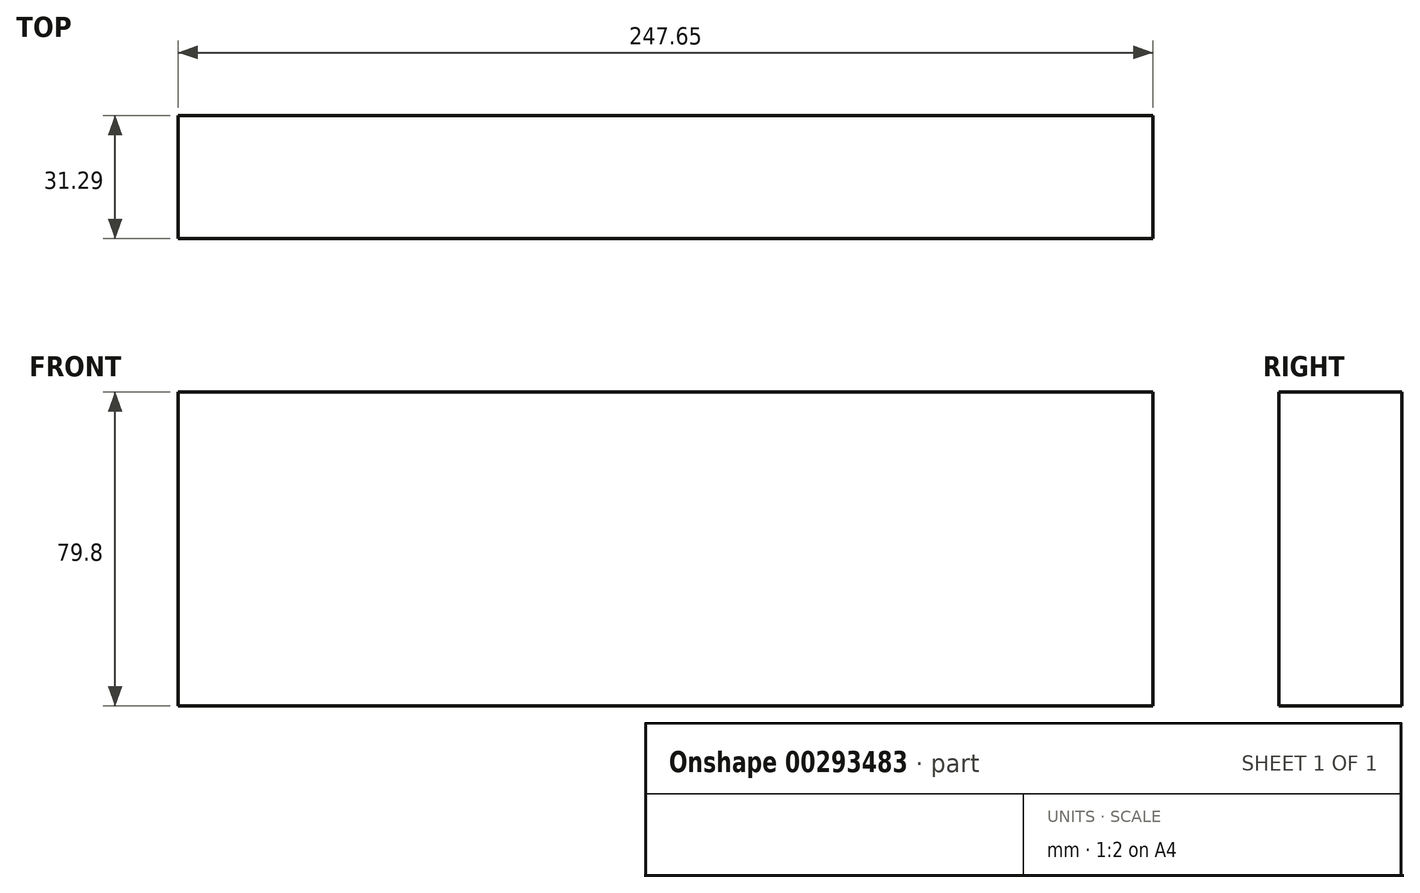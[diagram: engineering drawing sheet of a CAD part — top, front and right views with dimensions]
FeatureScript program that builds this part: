
annotation { "Feature Type Name" : "Feature", "Feature Type Description" : "" }
export const myFeature = defineFeature(function(context is Context, id is Id, definition is map)
    precondition{}
    {
        {
            var Q0;
            Q0=qCreatedBy(makeId("Front.planeOp"),FACE);
            var sketch = newSketch(context, id + "F0", { "sketchPlane" : qUnion([Q0])});
            skLineSegment(sketch, "E0.bottom", {"start": v(-81.04, 33.4) * mm, "end": v(166.6, 33.4) * mm});
            skLineSegment(sketch, "E0.top", {"start": v(-81.04, -46.41) * mm, "end": v(166.6, -46.41) * mm});
            skLineSegment(sketch, "E0.left", {"start": v(-81.04, 33.4) * mm, "end": v(-81.04, -46.41) * mm});
            skLineSegment(sketch, "E0.right", {"start": v(166.6, 33.4) * mm, "end": v(166.6, -46.41) * mm});
            skSolve(sketch);
        }
        {
            var Q0;
            Q0 = qSketchRegion(id + "F0", true);
            extrude(context, id + "F1", {"entities" : qUnion([Q0]), "depth" : 31.3 * mm});
        }
    });
